# Revit family: PlumbingFixture_GroheLimited_EuroCeramicWallhungWC_39328000_METRIC1
name_source: partatom
category: Plumbing Fixtures
revit_build: Autodesk Revit 2015 (Build: 20160512_1515(x64)
units: mm (PartAtom-declared; Revit-internal decimal feet)

## types (1)
- 39328000
    ADACompliant = No
    Assembly Code = N2010
    AssetType = Fixed
    BIMObjectName = PlumbingFixture_GroheLimited_EuroCeramicWallhungWC _39328000_METRIC
    CW Connection = No
    CWFU = 4.5
    ClassificationName = Uniclass2015
    ClassificationValue = Pr_40_20_93_94
    ColdWaterConnectionDiameter = 10 mm  [stored 0.0328084 ft]
    Color = White
    Cost = 0 $
    Description = Euro Ceramic Wallhung WC, Triple vortex, Rimless, Flushing volume 5/ 3L, Incl. fixation set , Optional Proguard & HyperClean (00H), Vitreous china, Alpine White, 16 pcs per pallet
    DurationUnit = Years
    Ecojoy = No
    ExpectedLife = 0
    Features = Euro Ceramic Wallhung WC, Triple vortex, Rimless, Flushing volume 5/ 3L, Incl. fixation set , Optional Proguard & HyperClean (00H), Vitreous china, Alpine White, 16 pcs per pallet
    Finish = Ceramic
    Grade = 2017
    HW Connection = No
    HWFU = 4.5
    HotWaterConnectionDiameter = 10 mm  [stored 0.0328084 ft]
    IfcExportAs = IfcPipeFitting
    IfcExportType = IfcPipeFittingType
    Keynote = N13
    LowEmittingMaterial = No
    Manufacturer = Grohe Limited
    ManufacturerName = Grohe Limited
    MasterformatNumber = 01 52 19
    MasterformatTitle = Sanitary Facilities
    Material = Ceramic
    Model = Euro Ceramic wallhung WC
    ModelNumber = 39328000
    ModelReference = Euro Ceramic wallhung WC
    NBSDescription = WC pans
    NBSObjectName = Grohe Limited -  WC pans
    NBSReference = 45-35-70/384
    NominalDepth = 0 mm  [stored 0 ft]
    NominalHeight = 0 mm  [stored 0 ft]
    NominalLength = 0 mm  [stored 0 ft]
    PrimaryMaterial = Ceramic, White
    ProductDocumentationLink = https://cdn.cloud.grohe.com
    ProductPageURL = https://www.grohe.co.uk
    ProductionYear = 2017
    Type Comments = 39328000
    TypeName = Euro Ceramic wallhung WC
    URL = www.grohe.com
    Vent Connection = No
    WFU = 0
    WarrantyDurationUnit = Years
    Waste Connection = Yes
    _BSBibleVersion = 14
    _BimSpecGuid = 0
    _CurrentRevision = 0
    _DistributedBy = www.bimstore.co.uk

note: [stored X ft] marks values corroborated as IEEE doubles in the binary element streams (Revit-internal decimal feet)

## geometry (parser evidence)
native form markers: Sweep x4
no freeform markers — native parametric forms only
